# Revit family: 2-6164-124 Dione
name_source: partatom
category: Lighting Fixtures
revit_build: Autodesk Revit LT 2014 (Build: 20130308_1515(x64)
units: mm (PartAtom-declared; Revit-internal decimal feet)

## types (1)
- 2-6164-124 Dione
    Apparent Load = 25 VA
    Ballast Manufacturer = Fulham RH3-UNV-226-C
    Color Filter = 16777215
    Default Elevation = 4' - 0"
    Description = 15" dia. ceiling mount
    Diffuser = 1 - Frosted Glass
    Dimming Lamp Color Temperature Shift = <None>
    Emit Shape Visible in Rendering = No
    Emit from Circle Diameter = 2' - 0"
    Fixture Diameter = 1' - 2 7/8"
    Fixture Height = 0' - 2 1/2"
    Input Power (Watts) = 24.8
    Input Voltage (Volts AC) = 120
    Junction Box = 4" Octagonal
    Lamp = 1x22W T-5 Circular Fluorescent
    Lamp Manufacturer = Sylvania FPC22/830
    Manufacturer = Oxygen Lighting
    Metal Finish = 24 - Satin Nickel
    Model = 2-6164-124
    Photometric Web File = 2-6164-124 Dione 15 ITL77200.IES
    Power Factor = 0.99
    Product Documentation Link = http://oxygenlighting.com.s3.amazonaws.com
    Tilt Angle = -90.00°
    Type Comments = Lighting- Fluorescent
    URL = http://www.oxygenlighting.com

## geometry (parser evidence)
native form markers: Sweep x1
no freeform markers — native parametric forms only
